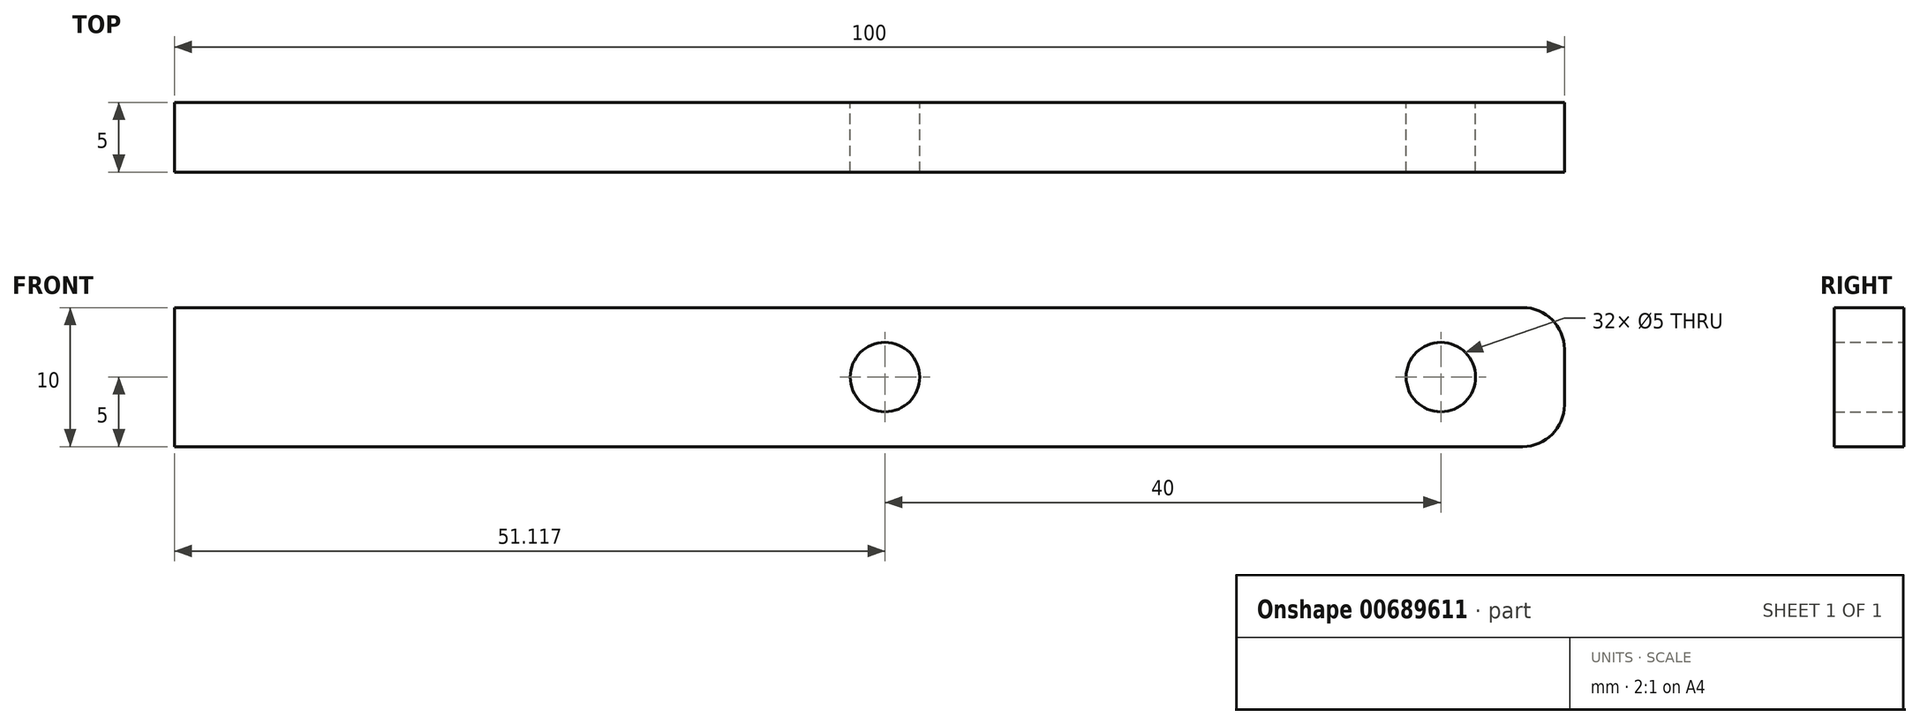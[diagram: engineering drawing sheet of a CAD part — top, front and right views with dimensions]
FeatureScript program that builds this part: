
annotation { "Feature Type Name" : "Feature", "Feature Type Description" : "" }
export const myFeature = defineFeature(function(context is Context, id is Id, definition is map)
    precondition{}
    {
        {
            var Q0;
            Q0=qCreatedBy(makeId("Front.planeOp"),FACE);
            var sketch = newSketch(context, id + "F0", { "sketchPlane" : qUnion([Q0])});
            skLineSegment(sketch, "E0.bottom", {"start": v(0, 0) * mm, "end": v(97, 0) * mm});
            skLineSegment(sketch, "E0.top", {"start": v(0, 10) * mm, "end": v(97, 10) * mm});
            skLineSegment(sketch, "E0.left", {"start": v(0, 0) * mm, "end": v(0, 10) * mm});
            skLineSegment(sketch, "E0.right", {"start": v(100, 3) * mm, "end": v(100, 7) * mm});
            skCircle(sketch, "E1", {"center": v(91.12, 5) * mm, "radius": 2.5 * mm});
            skCircle(sketch, "E2", {"center": v(51.12, 5) * mm, "radius": 2.5 * mm});
            skPoint(sketch, "E3.visualSharp", {"position": v(100, 10) * mm});
            skArc(sketch, "E3.filletArc", {"start": v(100, 7) * mm, "mid": v(99.12, 9.12) * mm, "end": v(97, 10) * mm});
            skPoint(sketch, "E4.visualSharp", {"position": v(100, 0) * mm});
            skArc(sketch, "E4.filletArc", {"start": v(97, 0) * mm, "mid": v(99.12, 0.88) * mm, "end": v(100, 3) * mm});
            skSolve(sketch);
        }
        {
            var Q0;
            Q0=makeQuery(id+"F0.imprint","IMPRINT",FACE,{"disambiguationData":[TD([[makeQuery(id+"F0.imprint","IMPRINT",EDGE,{"derivedFrom":sQuery(id+"F0.wireOp",EDGE,"E0.bottom")}),1.0]])]});
            extrude(context, id + "F1", {"entities" : qUnion([Q0]), "depth" : 5 * mm, "offsetDistance" : 25 * mm});
        }
    });
